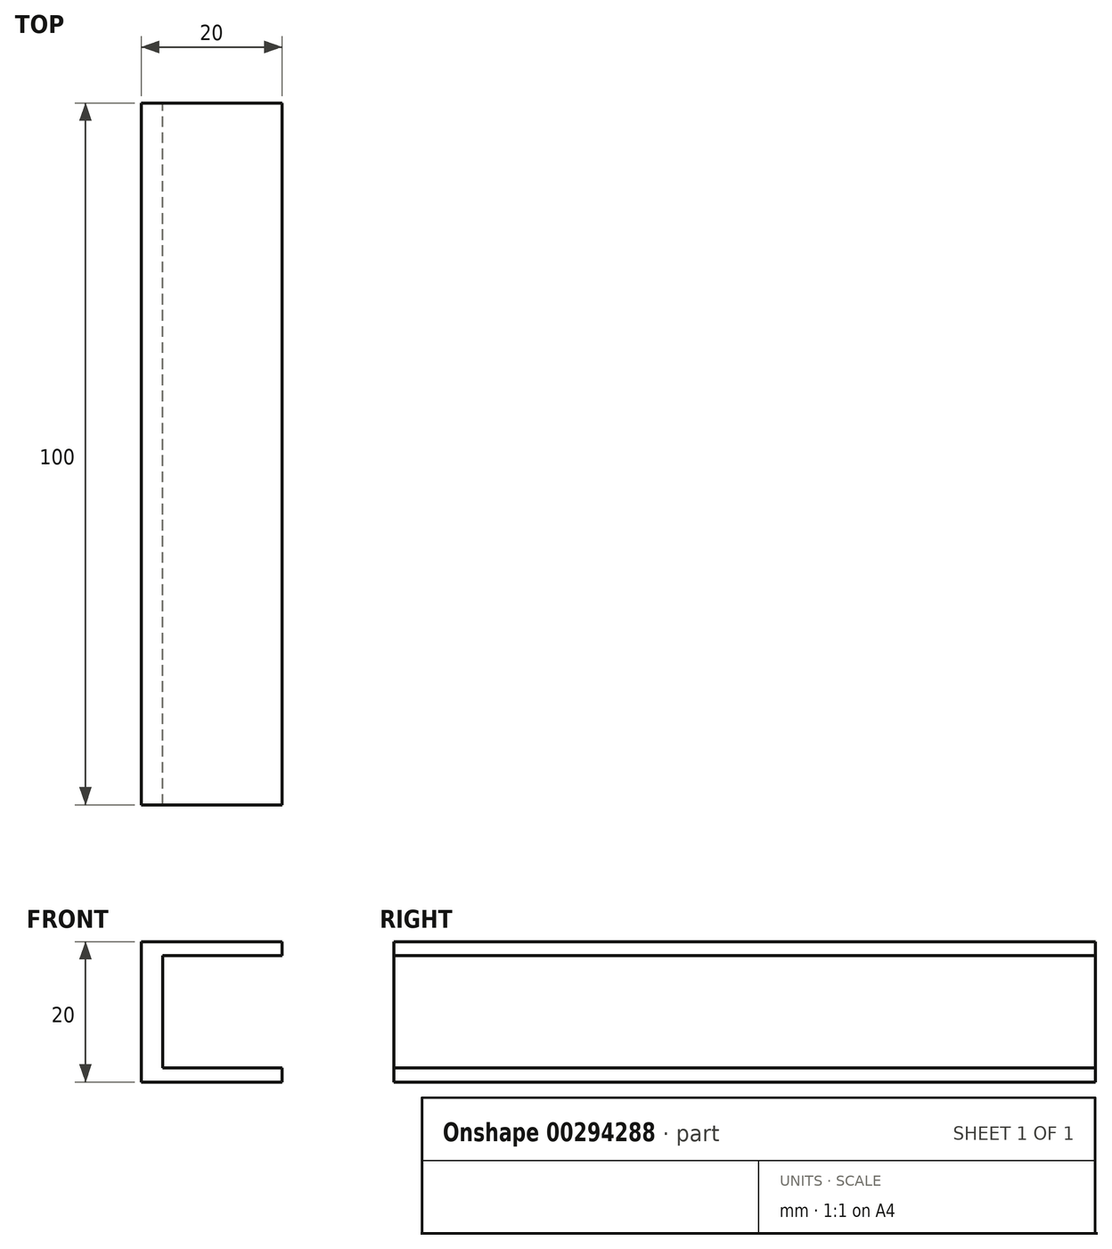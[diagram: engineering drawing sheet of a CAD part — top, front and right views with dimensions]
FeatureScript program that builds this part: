
annotation { "Feature Type Name" : "Feature", "Feature Type Description" : "" }
export const myFeature = defineFeature(function(context is Context, id is Id, definition is map)
    precondition{}
    {
        {
            var Q0;
            Q0=qCreatedBy(makeId("Front.planeOp"),FACE);
            var sketch = newSketch(context, id + "F0", { "sketchPlane" : qUnion([Q0])});
            skLineSegment(sketch, "E0.bottom", {"start": v(0, 0) * mm, "end": v(-20, 0) * mm});
            skLineSegment(sketch, "E0.top", {"start": v(0, 20) * mm, "end": v(-20, 20) * mm});
            skLineSegment(sketch, "E0.right", {"start": v(-20, 0) * mm, "end": v(-20, 20) * mm});
            skLineSegment(sketch, "E1", {"start": v(0, 18) * mm, "end": v(-17, 18) * mm});
            skLineSegment(sketch, "E2", {"start": v(-17, 18) * mm, "end": v(-17, 2) * mm});
            skLineSegment(sketch, "E3", {"start": v(-17, 2) * mm, "end": v(0, 2) * mm});
            skLineSegment(sketch, "E4", {"start": v(0, 20) * mm, "end": v(0, 18) * mm});
            skLineSegment(sketch, "E5.trimOffspring", {"start": v(0, 2) * mm, "end": v(0, 0) * mm});
            skSolve(sketch);
        }
        {
            var Q0;
            Q0 = qSketchRegion(id + "F0", true);
            extrude(context, id + "F1", {"entities" : qUnion([Q0]), "depth" : 100 * mm});
        }
    });
